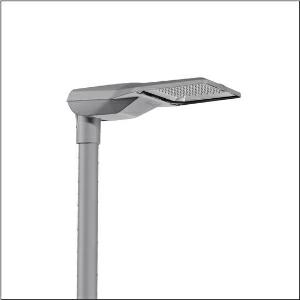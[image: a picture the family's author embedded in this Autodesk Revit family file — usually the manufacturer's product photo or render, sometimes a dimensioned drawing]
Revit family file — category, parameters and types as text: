
# Revit family: streetlight_sl_21_iq_midi___stw1_0a_5xe3e41d08mb_aeb4
name_source: partatom
category: Lighting Fixtures
units: mm (PartAtom-declared; Revit-internal decimal feet)

## family parameters
Cut with Voids When Loaded = No
Host = Face
Light Source = No
Part Type = Normal
Room Calculation Point = No
Round Connector Dimension = Use Diameter
Shared = No

## types (1)
- --- (1 x LED, 20360 lm, 146.7 W, 4000K)
    Apparent Load = 147 VA
    CIE Flux Codes = 38 75 98 100 100
    Color Rendering = 70
    Color Temperature = 4000K
    Default Elevation = 1800 mm
    Description = Streetlight SL 21 iQ midi, mast luminaire, primary light control with lens, of PMMA, primary optical cover: cover, of toughened safety glass, transparent, light distribution: STW1.0a, light emission: direct distribution, primary light characteristic: asymmetric, installation type: post-top, side-entry, LED, High Power LED, rated luminous flux: 20.360lm, luminous efficacy: 139lm/W, light colour: 740, colour temperature: 4000K, control: Auto-Match, Temp-Guard, Lumen-Switch, Night-Set, Smart-Wire, Light-Fading, Desk-Remote (wireless, voltage-free reading and setting of iQ features in the workshop via application-optimized NFC function/RFID function), optimised constant luminous flux control (CLO 2.0), presetting dimming linear, mains connection: 230..240V, AC, 50/60Hz, start of lifetime: 147W, end of service life: 161W, reduction: 62W, luminaire housing, of diecast aluminium, powder-coated, Siteco® metallic grey (DB 702S), corrosivity category C5 mid according to DIN EN ISO 12944, please order mast flange separately, inclination adjustable: 0°, 5°, 10°, 15°, sealing non-destructively replaceable, multi-level sealing system, length: 644mm, width: 335mm, height: 110mm, mast flange for spigot size: 42mm (side-entry): 5XC10008XM4, 60/48mm (side-entry/post-top): 5XC10108XM2, 76/60mm (side-entry/post-top): 5XC10108XM1, protection rating (complete): IP66, insulation class (complete): insulation class II (safety insulation), certification: CE, ENEC, ENEC+, VDE, impact resistance: IK09, permissible operating ambient temperature for outdoor applications: -40..+50°C, standard-compliant lighting for roads and squares, packaging unit: 1 piece

Light Distribution: STW1.0a
    Height = 111 mm
    Lamp = 1 x LED
    Lamp Light Flux = 20360 lm
    Lamp Power = 146.7 W
    Lamp count = 1
    Length = 644 mm
    Luminous efficacy = 139 lm/W
    Manufacturer = Siteco
    ModVariant = No
    Model = 5XE3E41D08MB
    Number of Poles = 1
    OnlyDefault = Yes
    Power Factor = 1
    Product Name = Streetlight SL 21 iQ midi | STW1.0a
    Product group = mast luminaire | pylon top
    ProductGroupID = 6100
    Protection Class = Protection class II
    Protection Degree = IP 66
    RLX_Detail_Level = 1
    RLX_Emergency_Light_Flux = 0 lm
    RLX_Emergency_Type = 0
    RLX_Emergency_Type_DB = No
    RlxData = <blob elided: 91229 chars, md5=958a9ffc>
    Socket = socket
    Standby Power = 0 W
    System Light Flux = 20360 lm
    System Power = 147 W
    Type Comments = factory setting: luminous flux: 100 % | dim-lin: 254 | 753 mA
    Type Image = l_1004298.jpg
    URL = http://relux.com
    VarID = @adj_121787
    Voltage = 0 V
    Weight = 0.00 kg
    Width = 336 mm

## geometry (parser evidence)
native form markers: Blend x4, Sweep x13
no freeform markers — native parametric forms only
